# Revit family: Стол медицинский нержавеющая сталь, с бортом, без борта
name_source: partatom
category: Оборудование
revit_build: Autodesk Revit 2017 (Build: 20170118_1100(x64)
units: mm (PartAtom-declared; Revit-internal decimal feet)

## family parameters
Всегда вертикально = Да
На основе рабочей плоскости = Нет
Общий = Нет
При загрузке вырезать с полостями = Нет
Размер круглого соединителя = Использовать диаметр
Тип детали = Нормальный
Точка расчета площади = Нет

## types (20) — shared parameters
Общ_Высота = 850 мм
Общ_Единицы измерения = шт.
Общ_Поставщик = БТ-Мебель

## per-type parameters (varying)
| type | Борт | Общ_Глубина | Общ_Наименование | Общ_Тип, марка | Общ_Ширина |
| 800х600х850 ББ | Нет | 600 мм | Стол медицинский из нержавеющей стали, без борта | БТ-С-6-8 | 800 мм |
| 800х700х850 ББ | Нет | 700 мм | Стол медицинский из нержавеющей стали, без борта | БТ-С-7-8 | 800 мм |
| 1000х600х850 ББ | Нет | 600 мм | Стол медицинский из нержавеющей стали, без борта | БТ-С-6-10 | 1000 мм |
| 1000х700х850 ББ | Нет | 700 мм | Стол медицинский из нержавеющей стали, без борта | БТ-С-7-10 | 1000 мм |
| 1200х600х850 ББ | Нет | 600 мм | Стол медицинский из нержавеющей стали, без борта | БТ-С-6-12 | 1200 мм |
| 1200х700х850 ББ | Нет | 700 мм | Стол медицинский из нержавеющей стали, без борта | БТ-С-7-12 | 1200 мм |
| 1400х600х850 ББ | Нет | 700 мм | Стол медицинский из нержавеющей стали, без борта | БТ-С-6-14 | 1400 мм |
| 1400х700х850 ББ | Нет | 700 мм | Стол медицинский из нержавеющей стали, без борта | БТ-С-7-14 | 1400 мм |
| 1500х600х850 ББ | Нет | 600 мм | Стол медицинский из нержавеющей стали, без борта | БТ-С-6-15 | 1500 мм |
| 1500х700х850 ББ | Нет | 700 мм | Стол медицинский из нержавеющей стали, без борта | БТ-С-7-15 | 1500 мм |
| 800х600х850 СБ | Да | 600 мм | Стол медицинский из нержавеющей стали, с бортом | БТ-СБ-6-8 | 800 мм |
| 800х700х850 СБ | Да | 700 мм | Стол медицинский из нержавеющей стали, с бортом | БТ-СБ-7-8 | 800 мм |
| 1000х600х850 СБ | Да | 600 мм | Стол медицинский из нержавеющей стали, с бортом | БТ-СБ-6-10 | 1000 мм |
| 1000х700х850 СБ | Да | 700 мм | Стол медицинский из нержавеющей стали, с бортом | БТ-СБ-7-10 | 1000 мм |
| 1200х600х850 СБ | Да | 600 мм | Стол медицинский из нержавеющей стали, с бортом | БТ-СБ-6-12 | 1200 мм |
| 1200х700х850 СБ | Да | 700 мм | Стол медицинский из нержавеющей стали, с бортом | БТ-СБ-7-12 | 1200 мм |
| 1400х600х850 СБ | Да | 600 мм | Стол медицинский из нержавеющей стали, с бортом | БТ-СБ-6-14 | 1400 мм |
| 1400х700х850 СБ | Да | 700 мм | Стол медицинский из нержавеющей стали, с бортом | БТ-СБ-7-14 | 1400 мм |
| 1500х600х850 СБ | Да | 600 мм | Стол медицинский из нержавеющей стали, с бортом | БТ-СБ-6-15 | 1500 мм |
| 1500х700х850 СБ | Да | 700 мм | Стол медицинский из нержавеющей стали, с бортом | БТ-СБ-7-15 | 1500 мм |
